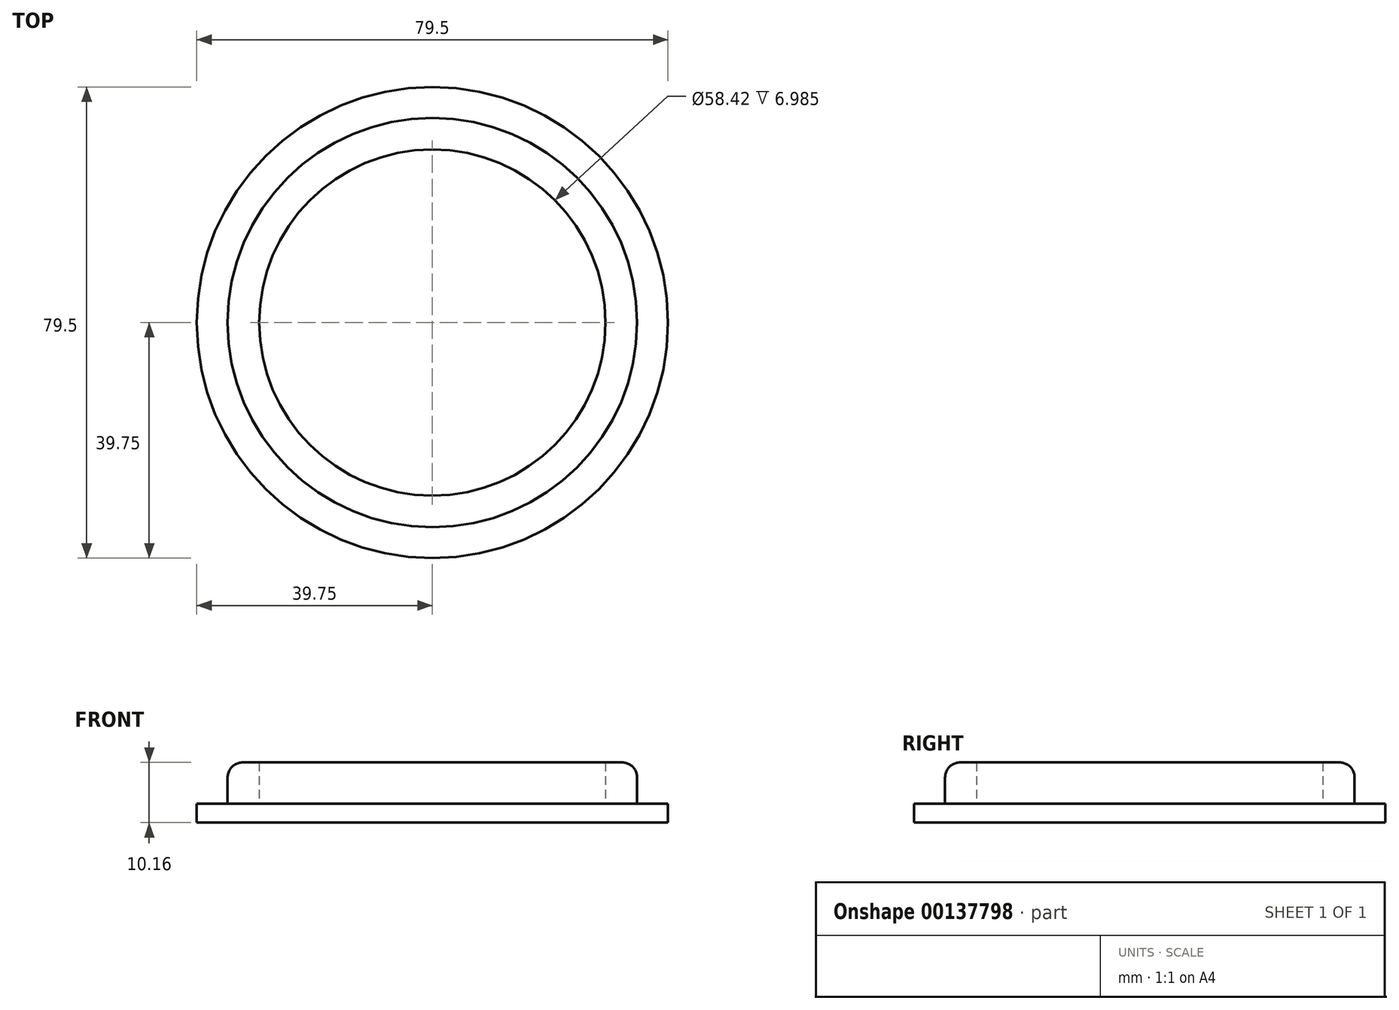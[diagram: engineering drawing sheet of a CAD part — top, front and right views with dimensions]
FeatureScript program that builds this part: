
annotation { "Feature Type Name" : "Feature", "Feature Type Description" : "" }
export const myFeature = defineFeature(function(context is Context, id is Id, definition is map)
    precondition{}
    {
        {
            var Q0;
            Q0=qCreatedBy(makeId("Top.planeOp"),FACE);
            var sketch = newSketch(context, id + "F0", { "sketchPlane" : qUnion([Q0])});
            skCircle(sketch, "E0", {"center": v(0, 0) * mm, "radius": 39.75 * mm});
            skCircle(sketch, "E1", {"center": v(0, 0) * mm, "radius": 34.54 * mm});
            skCircle(sketch, "E2", {"center": v(0, 0) * mm, "radius": 29.21 * mm});
            skSolve(sketch);
        }
        {
            var Q0;
            Q0=makeQuery(id+"F0.imprint","IMPRINT",FACE,{"disambiguationData":[TD([[makeQuery(id+"F0.imprint","IMPRINT",EDGE,{"derivedFrom":sQuery(id+"F0.wireOp",EDGE,"E0")}),1.0]])]});
            var Q1;
            Q1=makeQuery(id+"F0.imprint","IMPRINT",FACE,{"disambiguationData":[TD([[makeQuery(id+"F0.imprint","IMPRINT",EDGE,{"derivedFrom":sQuery(id+"F0.wireOp",EDGE,"E2")}),1.0]])]});
            extrude(context, id + "F1", {"entities" : qUnion([Q0, Q1]), "depth" : 3.17 * mm});
        }
        {
            var Q0;
            Q0=makeQuery(id+"F0.imprint","IMPRINT",FACE,{"disambiguationData":[TD([[makeQuery(id+"F0.imprint","IMPRINT",EDGE,{"derivedFrom":sQuery(id+"F0.wireOp",EDGE,"E1")}),1.0]])]});
            extrude(context, id + "F2", {"entities" : qUnion([Q0]), "operationType" : NewBodyOperationType.ADD, "depth" : 10.16 * mm});
        }
        {
            var Q0;
            Q0=makeQuery(id+"F2.opExtrude","CAP_EDGE",EDGE,{"disambiguationData":[OSD([sQuery(id+"F0.wireOp",EDGE,"E1")])],"isStart":false});
            fillet(context, id + "F3", {"entities" : qUnion([Q0]), "radius" : 2.54 * mm, "tangentPropagation" : true, "allowEdgeOverflow" : false});
        }
    });
